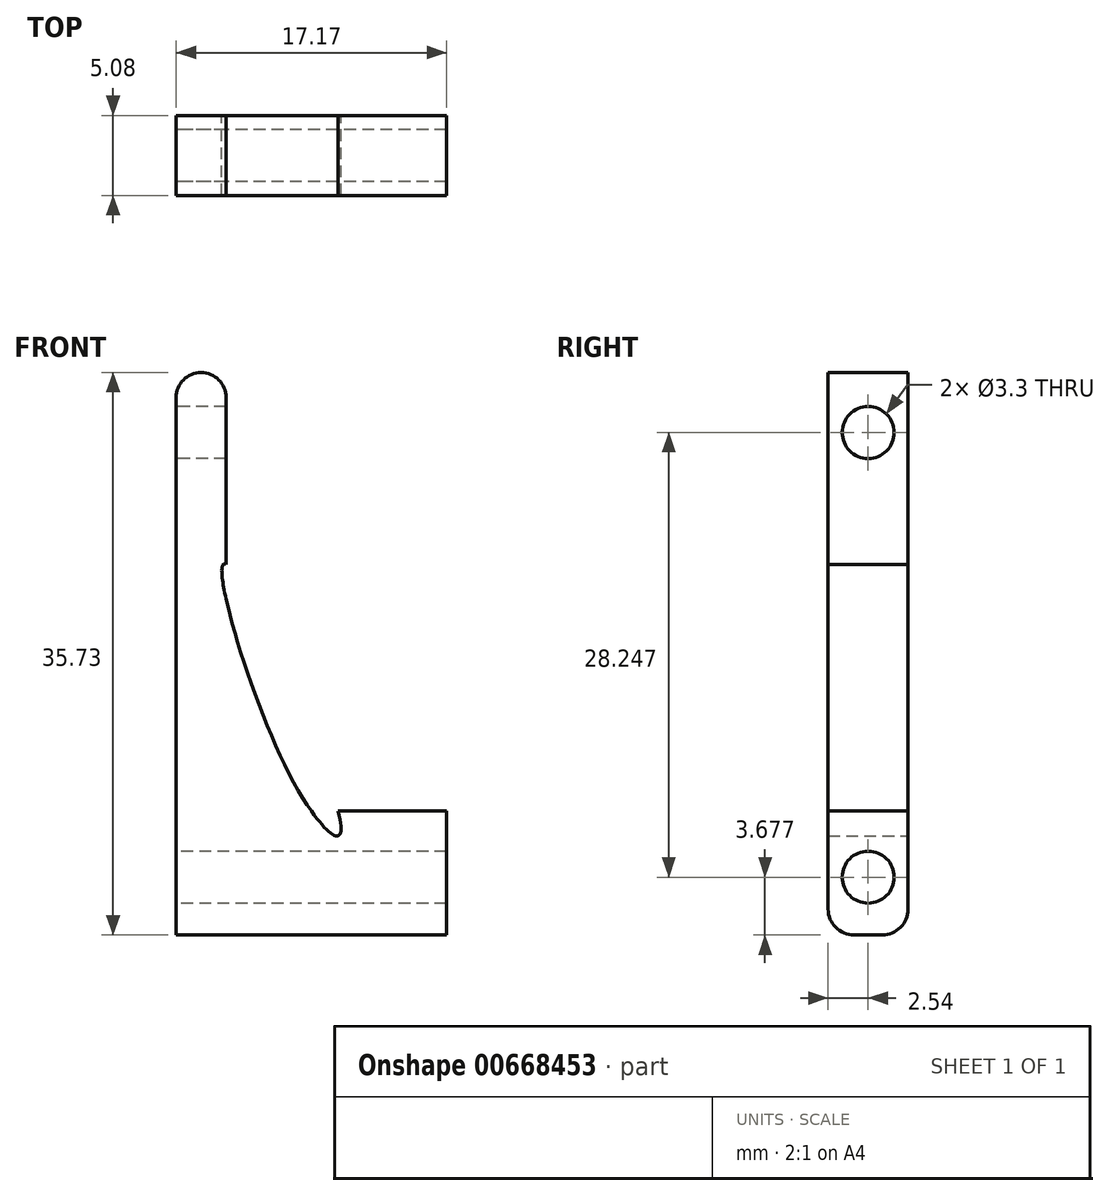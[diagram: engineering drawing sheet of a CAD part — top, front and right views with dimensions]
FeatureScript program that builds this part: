
annotation { "Feature Type Name" : "Feature", "Feature Type Description" : "" }
export const myFeature = defineFeature(function(context is Context, id is Id, definition is map)
    precondition{}
    {
        {
            var Q0;
            Q0=qCreatedBy(makeId("Front.planeOp"),FACE);
            var sketch = newSketch(context, id + "F0", { "sketchPlane" : qUnion([Q0])});
            skLineSegment(sketch, "E0", {"start": v(-26.62, 37.14) * mm, "end": v(-26.62, 44.22) * mm});
            skLineSegment(sketch, "E1", {"start": v(-23.45, 44.22) * mm, "end": v(-23.45, 37.14) * mm});
            skLineSegment(sketch, "E2", {"start": v(-25.04, 45.42) * mm, "end": v(-24.64, 45.42) * mm});
            skFitSpline(sketch, "E3.MirrorCS", {"points": [v(-16.15, 22.5) * mm, v(-19.25, 25.66) * mm, v(-23.45, 39.33) * mm, v(-16.15, 22.5) * mm]});
            skLineSegment(sketch, "E4", {"start": v(-26.62, 15.8) * mm, "end": v(-18.03, 15.8) * mm});
            skLineSegment(sketch, "E5", {"start": v(-26.62, 37.14) * mm, "end": v(-26.62, 15.8) * mm});
            skLineSegment(sketch, "E6", {"start": v(-18.03, 23.66) * mm, "end": v(-9.45, 23.66) * mm});
            skLineSegment(sketch, "E7", {"start": v(-9.45, 23.66) * mm, "end": v(-9.45, 15.8) * mm});
            skLineSegment(sketch, "E8", {"start": v(-9.45, 15.8) * mm, "end": v(-18.03, 15.8) * mm});
            skPoint(sketch, "E9.orphan", {"position": v(-32.26, 15.8) * mm});
            skLineSegment(sketch, "E10", {"start": v(-26.62, 44.22) * mm, "end": v(-26.62, 49.93) * mm});
            skLineSegment(sketch, "E11", {"start": v(-23.45, 49.93) * mm, "end": v(-23.45, 44.22) * mm});
            skArc(sketch, "E12", {"start": v(-23.45, 49.93) * mm, "mid": v(-25.04, 51.52) * mm, "end": v(-26.62, 49.93) * mm});
            skSolve(sketch);
        }
        {
            var Q0;
            Q0=makeQuery(id+"F0.imprint","IMPRINT",FACE,{"disambiguationData":[TD([[makeQuery(id+"F0.imprint","IMPRINT",EDGE,{"derivedFrom":sQuery(id+"F0.wireOp",EDGE,"E0")}),-1.0]])]});
            extrude(context, id + "F1", {"entities" : qUnion([Q0]), "depth" : 5.08 * mm});
        }
        {
            var Q0;
            Q0=makeQuery(id+"F1.opExtrude","CAP_EDGE",EDGE,{"disambiguationData":[OSD([sQuery(id+"F0.wireOp",EDGE,"E4"),sQuery(id+"F0.wireOp",EDGE,"E8")])],"isStart":false});
            var Q1;
            Q1=makeQuery(id+"F1.opExtrude","CAP_EDGE",EDGE,{"disambiguationData":[OSD([sQuery(id+"F0.wireOp",EDGE,"E4"),sQuery(id+"F0.wireOp",EDGE,"E8")])],"isStart":true});
            fillet(context, id + "F2", {"entities" : qUnion([Q0, Q1]), "radius" : 1.65 * mm, "tangentPropagation" : true, "allowEdgeOverflow" : false});
        }
        {
            var Q0;
            Q0=makeQuery(id+"F1.opExtrude","SWEPT_FACE",FACE,{"disambiguationData":[OSD([sQuery(id+"F0.wireOp",EDGE,"E0"),sQuery(id+"F0.wireOp",EDGE,"E5"),sQuery(id+"F0.wireOp",EDGE,"E10")])]});
            var sketch = newSketch(context, id + "F3", { "sketchPlane" : qUnion([Q0])});
            skCircle(sketch, "E13", {"center": v(2.54, 19.47) * mm, "radius": 1.8 * mm});
            skCircle(sketch, "E14", {"center": v(2.54, 47.71) * mm, "radius": 1.75 * mm});
            skSolve(sketch);
        }
        {
            var Q0;
            Q0=sQuery(id+"F3.wireOp",VERTEX,"E14.center");
            var Q1;
            Q1=sQuery(id+"F3.wireOp",VERTEX,"E13.center");
            var Q2;
            Q2=makeQuery(id+"F1.opExtrude","SWEPT_BODY",BODY,{"disambiguationData":[OSD([sQuery(id+"F0.wireOp",EDGE,"E0"),sQuery(id+"F0.wireOp",EDGE,"E1"),sQuery(id+"F0.wireOp",EDGE,"E3.MirrorCS"),sQuery(id+"F0.wireOp",EDGE,"E4"),sQuery(id+"F0.wireOp",EDGE,"E5"),sQuery(id+"F0.wireOp",EDGE,"E6"),sQuery(id+"F0.wireOp",EDGE,"E7"),sQuery(id+"F0.wireOp",EDGE,"E8"),sQuery(id+"F0.wireOp",EDGE,"E10"),sQuery(id+"F0.wireOp",EDGE,"E11"),sQuery(id+"F0.wireOp",EDGE,"E12")])]});
            hole(context, id + "F4", {"style" : HoleStyle.SIMPLE, "endStyle" : HoleEndStyle.THROUGH, "standardTappedOrClearance" : lookupTablePath({ "standard" : "ISO", "fit" : "Normal", "size" : "M3", "type" : "Clearance" }), "standardBlindInLast" : lookupTablePath({ "fit" : "Standard", "standard" : "ISO", "size" : "M3", "type" : "Clearance" }), "holeDiameter" : 3.3 * mm, "isTappedThrough" : true, "tappedDepth" : 12.7 * mm, "tapClearance" : 3, "locations" : qUnion([Q0, Q1]), "scope" : qUnion([Q2])});
        }
    });
